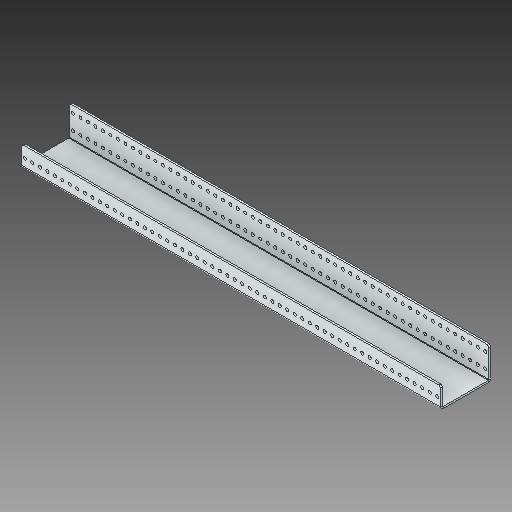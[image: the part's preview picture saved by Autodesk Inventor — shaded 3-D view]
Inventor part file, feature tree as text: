
AUTODESK INVENTOR PART (.ipt)
format: ipt  version: 2018 (Build 220112000, 112)  size: 274,432 bytes
history: native  units: in
note: dims shown in document units (in); Inventor stores cm internally (conversion verified against a paired STEP export)
features: chamfer x1
ambient origin geometry x8: Origin, YZ Plane, XZ Plane, XY Plane, X Axis, Y Axis, Z Axis, Center Point
bodies: Solid1 (feature_tree)
feature tree (1):
  chamfer  "Chamfer2"  [1 undecoded]
note: 1 required parameter value undecoded (feature->parameter linkage not recoverable at this tier; creation-order binding heuristic only, values carry confidence <= 0.55)
